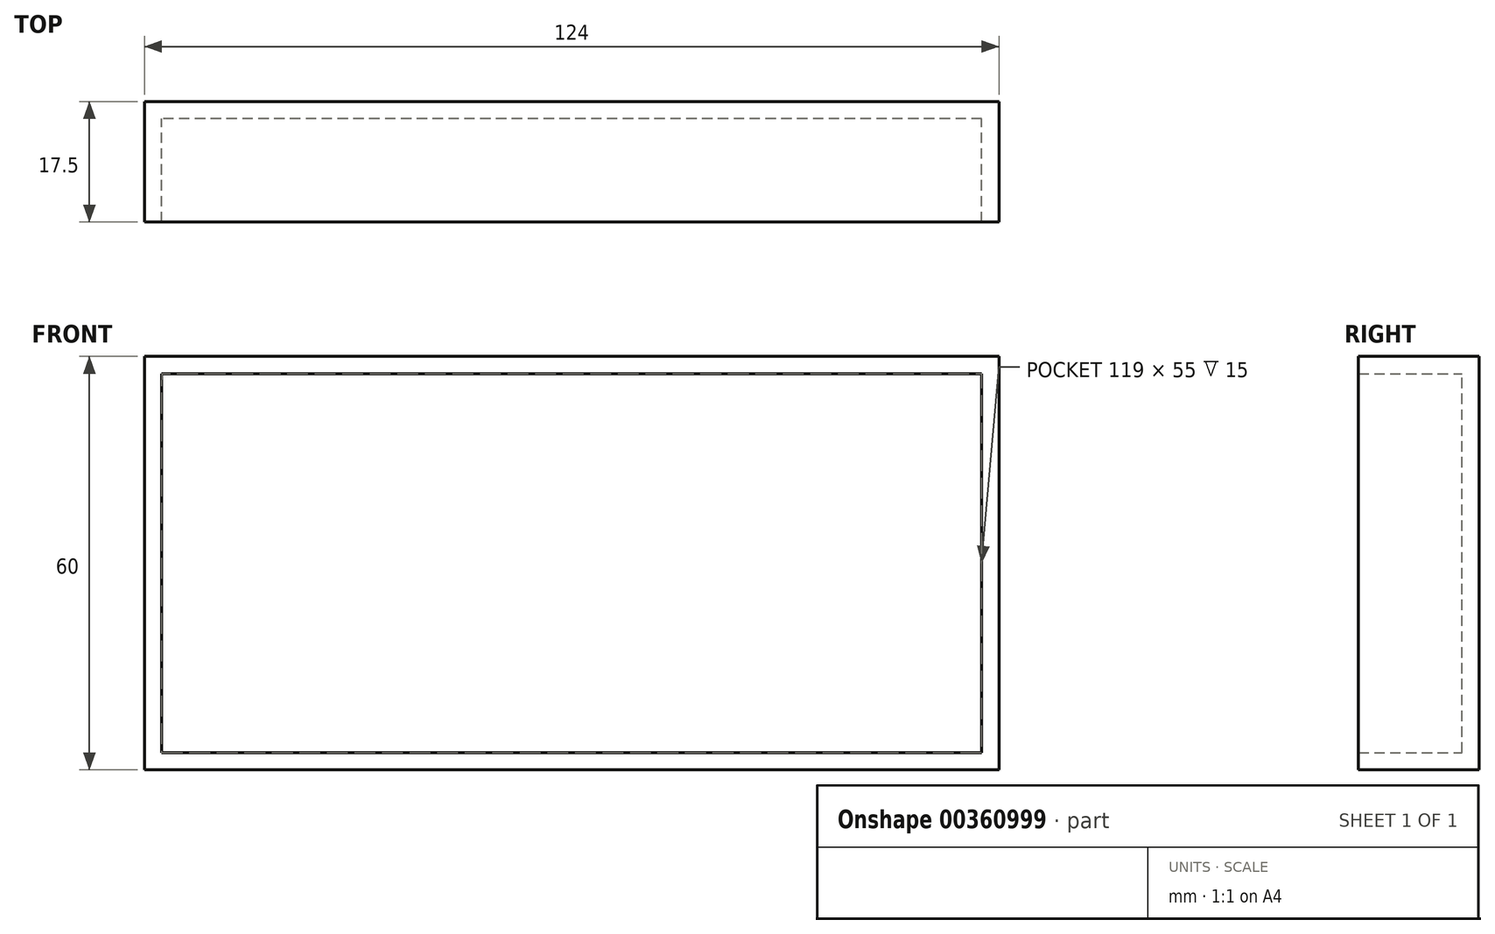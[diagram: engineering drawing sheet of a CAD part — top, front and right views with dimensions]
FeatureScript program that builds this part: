
annotation { "Feature Type Name" : "Feature", "Feature Type Description" : "" }
export const myFeature = defineFeature(function(context is Context, id is Id, definition is map)
    precondition{}
    {
        {
            var Q0;
            Q0=qCreatedBy(makeId("Front.planeOp"),FACE);
            var sketch = newSketch(context, id + "F0", { "sketchPlane" : qUnion([Q0])});
            skLineSegment(sketch, "E0.bottom", {"start": v(34.5, -27.5) * mm, "end": v(-34.5, -27.5) * mm});
            skLineSegment(sketch, "E0.top", {"start": v(34.5, 27.5) * mm, "end": v(-34.5, 27.5) * mm});
            skLineSegment(sketch, "E0.left", {"start": v(34.5, -27.5) * mm, "end": v(34.5, 27.5) * mm});
            skLineSegment(sketch, "E0.right", {"start": v(-34.5, -27.5) * mm, "end": v(-34.5, 27.5) * mm});
            skPoint(sketch, "E0.middle", {"position": v(0, 0) * mm});
            skSolve(sketch);
        }
        {
            var Q0;
            Q0 = qSketchRegion(id + "F0", true);
            extrude(context, id + "F1", {"entities" : qUnion([Q0]), "depth" : 15 * mm});
        }
        {
            var Q0;
            Q0=makeQuery(id+"F1.opExtrude","CAP_FACE",FACE,{"disambiguationData":[OSD([sQuery(id+"F0.wireOp",EDGE,"E0.bottom"),sQuery(id+"F0.wireOp",EDGE,"E0.top"),sQuery(id+"F0.wireOp",EDGE,"E0.left"),sQuery(id+"F0.wireOp",EDGE,"E0.right")])],"isStart":false});
            shell(context, id + "F2", {"entities" : qUnion([Q0]), "thickness" : 2.5 * mm, "oppositeDirection" : true});
        }
        {
            var Q0;
            Q0=makeQuery(id+"F1.opExtrude","SWEPT_FACE",FACE,{"disambiguationData":[OSD([sQuery(id+"F0.wireOp",EDGE,"E0.left")])]});
            extrude(context, id + "F3", {"entities" : qUnion([Q0]), "operationType" : NewBodyOperationType.ADD, "depth" : 50 * mm});
        }
        {
            var Q0;
            Q0=makeQuery(id+"F2.opShell","OFFSET_FACE",FACE,{"disambiguationData":[OSD([sQuery(id+"F0.wireOp",EDGE,"E0.left")])]});
            var Q1;
            {var subQ0=sQuery(id+"F0.wireOp",EDGE,"E0.left");Q1=makeQuery(id+"F3.boolean.opBoolean","MERGE",FACE,{"derivedFrom":[makeQuery(id+"F1.opExtrude","CAP_FACE",FACE,{"disambiguationData":[OSD([sQuery(id+"F0.wireOp",EDGE,"E0.bottom"),sQuery(id+"F0.wireOp",EDGE,"E0.top"),subQ0,sQuery(id+"F0.wireOp",EDGE,"E0.right")])],"isStart":false}),makeQuery(id+"F3.opExtrude","SWEPT_FACE",FACE,{"disambiguationData":[OSD([subQ0]),TDD([makeQuery(id+"F1.opExtrude","CAP_EDGE",EDGE,{"disambiguationData":[OSD([subQ0])],"isStart":false})])]})]});}
            shell(context, id + "F4", {"entities" : qUnion([Q0, Q1]), "thickness" : 2.5 * mm});
        }
    });
